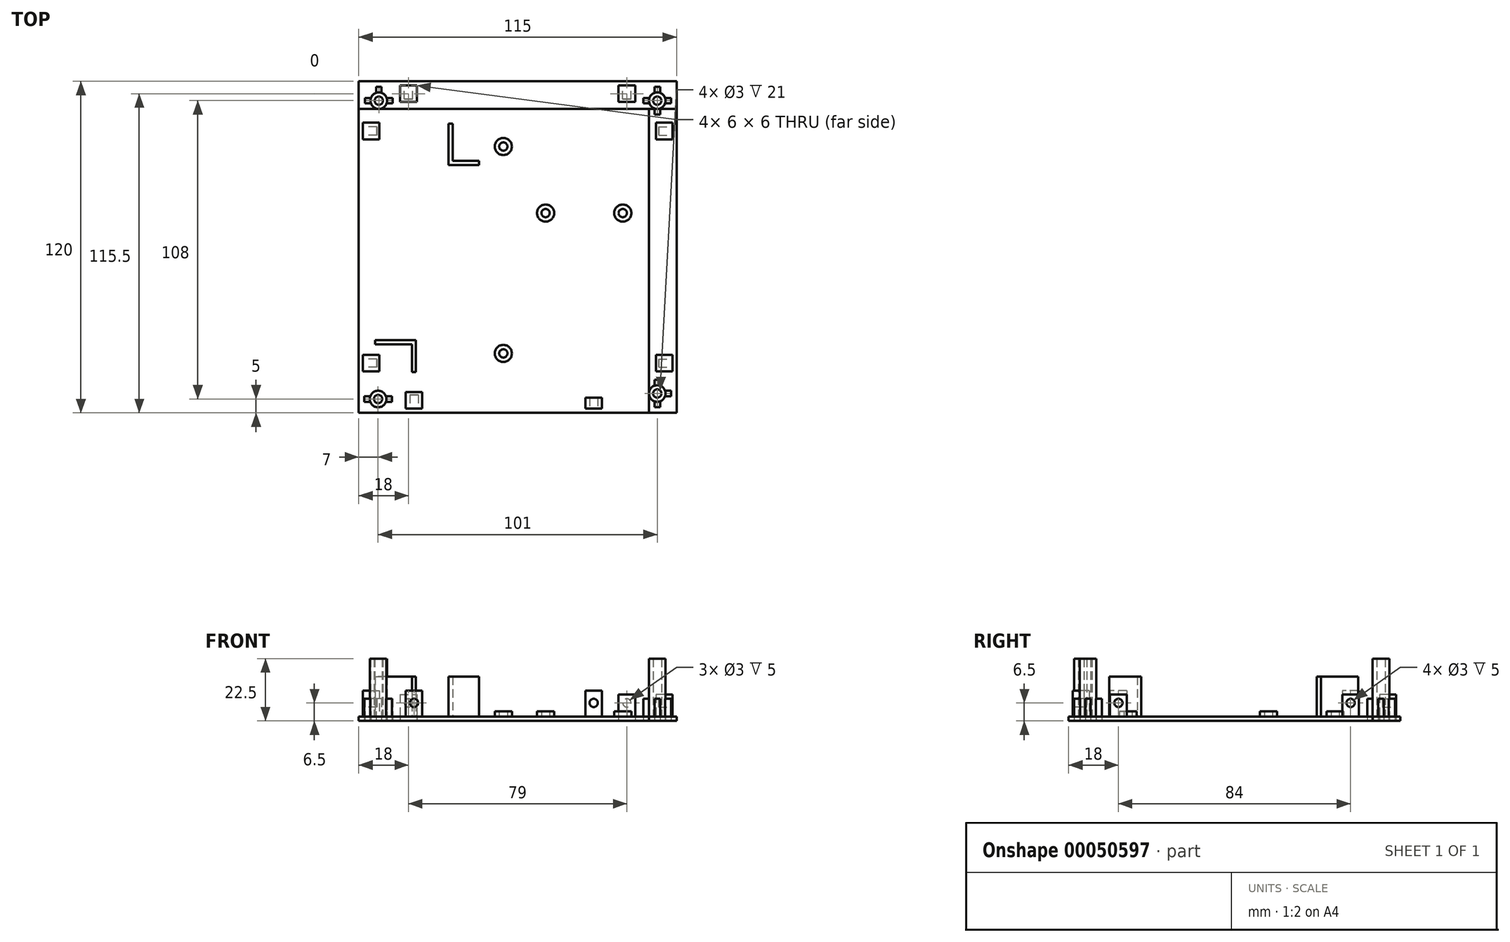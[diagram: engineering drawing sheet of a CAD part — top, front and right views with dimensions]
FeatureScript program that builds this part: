
annotation { "Feature Type Name" : "Feature", "Feature Type Description" : "" }
export const myFeature = defineFeature(function(context is Context, id is Id, definition is map)
    precondition{}
    {
        {
            var Q0;
            Q0=qCreatedBy(makeId("Top.planeOp"),FACE);
            var sketch = newSketch(context, id + "F0", { "sketchPlane" : qUnion([Q0])});
            skLineSegment(sketch, "E0.rect.bottom", {"start": v(52.5, 55) * mm, "end": v(-52.5, 55) * mm});
            skLineSegment(sketch, "E0.rect.top", {"start": v(52.5, -55) * mm, "end": v(-52.5, -55) * mm});
            skLineSegment(sketch, "E0.rect.left", {"start": v(52.5, 55) * mm, "end": v(52.5, -55) * mm});
            skLineSegment(sketch, "E0.rect.right", {"start": v(-52.5, 55) * mm, "end": v(-52.5, -55) * mm});
            skPoint(sketch, "E0.rect.middle", {"position": v(0, 0) * mm});
            skCircle(sketch, "E1", {"center": v(-45.5, -50) * mm, "radius": 3 * mm});
            skCircle(sketch, "E2", {"center": v(-45.5, -50) * mm, "radius": 1.5 * mm});
            skPoint(sketch, "E3.rect.middle", {"position": v(-45.5, -53) * mm});
            skLineSegment(sketch, "E4.rect.bottom", {"start": v(-50.5, -49) * mm, "end": v(-48.33, -49) * mm});
            skLineSegment(sketch, "E4.rect.top", {"start": v(-50.5, -51) * mm, "end": v(-48.33, -51) * mm});
            skLineSegment(sketch, "E4.rect.left", {"start": v(-50.5, -49) * mm, "end": v(-50.5, -51) * mm});
            skPoint(sketch, "E4.rect.middle", {"position": v(-48.5, -50) * mm});
            skLineSegment(sketch, "E5.rect.bottom", {"start": v(-40.5, -49) * mm, "end": v(-42.67, -49) * mm});
            skLineSegment(sketch, "E5.rect.top", {"start": v(-40.5, -51) * mm, "end": v(-42.67, -51) * mm});
            skLineSegment(sketch, "E5.rect.left", {"start": v(-40.5, -49) * mm, "end": v(-40.5, -51) * mm});
            skPoint(sketch, "E5.rect.middle", {"position": v(-42.5, -50) * mm});
            skPoint(sketch, "E4.rect.right.end.orphan", {"position": v(-46.5, -51) * mm});
            skPoint(sketch, "E6.trimOffspring.end.orphan", {"position": v(-46.5, -49) * mm});
            skPoint(sketch, "E7.orphan", {"position": v(-44.5, -49) * mm});
            skPoint(sketch, "E8.orphan", {"position": v(-44.5, -51) * mm});
            skSolve(sketch);
        }
        {
            var Q0;
            Q0=makeQuery(id+"F0.imprint","IMPRINT",FACE,{"disambiguationData":[TD([[makeQuery(id+"F0.imprint","IMPRINT",EDGE,{"derivedFrom":sQuery(id+"F0.wireOp",EDGE,"E0.rect.bottom")}),1.0]])]});
            extrude(context, id + "F1", {"entities" : qUnion([Q0]), "depth" : 1.5 * mm});
        }
        {
            var Q0;
            Q0=makeQuery(id+"F1.opExtrude","CAP_FACE",FACE,{"disambiguationData":[OSD([sQuery(id+"F0.wireOp",EDGE,"E0.rect.bottom"),sQuery(id+"F0.wireOp",EDGE,"E0.rect.top"),sQuery(id+"F0.wireOp",EDGE,"E0.rect.left"),sQuery(id+"F0.wireOp",EDGE,"E0.rect.right")])],"isStart":false});
            var sketch = newSketch(context, id + "F2", { "sketchPlane" : qUnion([Q0])});
            skCircle(sketch, "E9", {"center": v(-0.2, 41.4) * mm, "radius": 3.1 * mm});
            skCircle(sketch, "E10", {"center": v(-0.2, 41.4) * mm, "radius": 1.5 * mm});
            skCircle(sketch, "E11", {"center": v(-0.2, -33.5) * mm, "radius": 3.1 * mm});
            skCircle(sketch, "E12", {"center": v(-0.2, -33.5) * mm, "radius": 1.5 * mm});
            skCircle(sketch, "E13", {"center": v(43, 17.3) * mm, "radius": 3.1 * mm});
            skCircle(sketch, "E14", {"center": v(43, 17.3) * mm, "radius": 1.5 * mm});
            skCircle(sketch, "E15", {"center": v(15.1, 17.3) * mm, "radius": 3.1 * mm});
            skCircle(sketch, "E16", {"center": v(15.1, 17.3) * mm, "radius": 1.5 * mm});
            skLineSegment(sketch, "E17", {"start": v(-20, 49.73) * mm, "end": v(-20, 34.73) * mm});
            skLineSegment(sketch, "E18", {"start": v(-20, 34.73) * mm, "end": v(-9, 34.73) * mm});
            skLineSegment(sketch, "E19", {"start": v(-9, 34.73) * mm, "end": v(-9, 36.23) * mm});
            skLineSegment(sketch, "E20", {"start": v(-9, 36.23) * mm, "end": v(-18.5, 36.23) * mm});
            skLineSegment(sketch, "E21", {"start": v(-18.5, 36.23) * mm, "end": v(-18.5, 49.73) * mm});
            skLineSegment(sketch, "E22", {"start": v(-18.5, 49.73) * mm, "end": v(-20, 49.73) * mm});
            skLineSegment(sketch, "E23", {"start": v(-46.6, -28.7) * mm, "end": v(-31.8, -28.7) * mm});
            skLineSegment(sketch, "E24", {"start": v(-31.8, -28.7) * mm, "end": v(-31.8, -40.3) * mm});
            skLineSegment(sketch, "E25", {"start": v(-31.8, -40.3) * mm, "end": v(-33.3, -40.3) * mm});
            skLineSegment(sketch, "E26", {"start": v(-33.3, -40.3) * mm, "end": v(-33.3, -30.2) * mm});
            skLineSegment(sketch, "E27", {"start": v(-33.3, -30.2) * mm, "end": v(-46.6, -30.2) * mm});
            skLineSegment(sketch, "E28", {"start": v(-46.6, -30.2) * mm, "end": v(-46.6, -28.7) * mm});
            skSolve(sketch);
        }
        {
            var Q0;
            Q0=makeQuery(id+"F2.imprint","IMPRINT",FACE,{"disambiguationData":[TD([[makeQuery(id+"F2.imprint","IMPRINT",EDGE,{"derivedFrom":sQuery(id+"F2.wireOp",EDGE,"E9")}),1.0]])]});
            var Q1;
            Q1=makeQuery(id+"F2.imprint","IMPRINT",FACE,{"disambiguationData":[TD([[makeQuery(id+"F2.imprint","IMPRINT",EDGE,{"derivedFrom":sQuery(id+"F2.wireOp",EDGE,"E15")}),1.0]])]});
            var Q2;
            Q2=makeQuery(id+"F2.imprint","IMPRINT",FACE,{"disambiguationData":[TD([[makeQuery(id+"F2.imprint","IMPRINT",EDGE,{"derivedFrom":sQuery(id+"F2.wireOp",EDGE,"E13")}),1.0]])]});
            var Q3;
            Q3=makeQuery(id+"F2.imprint","IMPRINT",FACE,{"disambiguationData":[TD([[makeQuery(id+"F2.imprint","IMPRINT",EDGE,{"derivedFrom":sQuery(id+"F2.wireOp",EDGE,"E11")}),1.0]])]});
            extrude(context, id + "F3", {"entities" : qUnion([Q0, Q1, Q2, Q3]), "operationType" : NewBodyOperationType.ADD, "depth" : 2 * mm});
        }
        {
            var Q0;
            Q0=makeQuery(id+"F2.imprint","IMPRINT",FACE,{"disambiguationData":[TD([[makeQuery(id+"F2.imprint","IMPRINT",EDGE,{"derivedFrom":sQuery(id+"F2.wireOp",EDGE,"E17")}),1.0]])]});
            extrude(context, id + "F4", {"entities" : qUnion([Q0]), "operationType" : NewBodyOperationType.ADD, "depth" : 14.5 * mm});
        }
        {
            var Q0;
            Q0=makeQuery(id+"F2.imprint","IMPRINT",FACE,{"disambiguationData":[TD([[makeQuery(id+"F2.imprint","IMPRINT",EDGE,{"derivedFrom":sQuery(id+"F2.wireOp",EDGE,"E23")}),-1.0]])]});
            extrude(context, id + "F5", {"entities" : qUnion([Q0]), "operationType" : NewBodyOperationType.ADD, "depth" : 14.5 * mm});
        }
        {
            var Q0;
            Q0=qCreatedBy(makeId("Top.planeOp"),FACE);
            var sketch = newSketch(context, id + "F6", { "sketchPlane" : qUnion([Q0])});
            skLineSegment(sketch, "E29.bottom", {"start": v(-52.5, 55) * mm, "end": v(62.5, 55) * mm});
            skLineSegment(sketch, "E29.top", {"start": v(-52.5, 65) * mm, "end": v(62.5, 65) * mm});
            skLineSegment(sketch, "E29.left", {"start": v(-52.5, 55) * mm, "end": v(-52.5, 65) * mm});
            skLineSegment(sketch, "E29.right", {"start": v(62.5, 55) * mm, "end": v(62.5, 65) * mm});
            skLineSegment(sketch, "E30.bottom", {"start": v(62.5, 55) * mm, "end": v(52.5, 55) * mm});
            skLineSegment(sketch, "E30.top", {"start": v(62.5, -55) * mm, "end": v(52.5, -55) * mm});
            skLineSegment(sketch, "E30.left", {"start": v(62.5, 55) * mm, "end": v(62.5, -55) * mm});
            skLineSegment(sketch, "E30.right", {"start": v(52.5, 55) * mm, "end": v(52.5, -55) * mm});
            skCircle(sketch, "E31", {"center": v(-45.24, 58) * mm, "radius": 3 * mm});
            skCircle(sketch, "E32", {"center": v(-45.24, 58) * mm, "radius": 1.5 * mm});
            skLineSegment(sketch, "E33.rect.bottom", {"start": v(-44.24, 63) * mm, "end": v(-46.24, 63) * mm});
            skLineSegment(sketch, "E33.rect.left", {"start": v(-44.24, 63) * mm, "end": v(-44.24, 60.83) * mm});
            skLineSegment(sketch, "E33.rect.right", {"start": v(-46.24, 63) * mm, "end": v(-46.24, 60.83) * mm});
            skPoint(sketch, "E33.rect.middle", {"position": v(-45.24, 61) * mm});
            skLineSegment(sketch, "E34.rect.right", {"start": v(-50.24, 59) * mm, "end": v(-50.24, 57) * mm});
            skPoint(sketch, "E34.rect.middle", {"position": v(-48.24, 58) * mm});
            skLineSegment(sketch, "E35.rect.bottom", {"start": v(-44.24, 53) * mm, "end": v(-46.24, 53) * mm});
            skLineSegment(sketch, "E35.rect.left", {"start": v(-44.24, 53) * mm, "end": v(-44.24, 55.17) * mm});
            skLineSegment(sketch, "E35.rect.right", {"start": v(-46.24, 53) * mm, "end": v(-46.24, 55.17) * mm});
            skPoint(sketch, "E35.rect.middle", {"position": v(-45.24, 55) * mm});
            skLineSegment(sketch, "E36.rect.bottom", {"start": v(-40.24, 59) * mm, "end": v(-42.4, 59) * mm});
            skLineSegment(sketch, "E36.rect.top", {"start": v(-40.24, 57) * mm, "end": v(-42.4, 57) * mm});
            skLineSegment(sketch, "E36.rect.left", {"start": v(-40.24, 59) * mm, "end": v(-40.24, 57) * mm});
            skPoint(sketch, "E36.rect.middle", {"position": v(-42.24, 58) * mm});
            skPoint(sketch, "E37.trimOffspring.end.orphan", {"position": v(-44.24, 57) * mm});
            skLineSegment(sketch, "E38.trimOffspring", {"start": v(-48.06, 57) * mm, "end": v(-50.24, 57) * mm});
            skPoint(sketch, "E34.rect.top.start.orphan", {"position": v(-46.24, 57) * mm});
            skLineSegment(sketch, "E39.trimOffspring", {"start": v(-48.06, 59) * mm, "end": v(-50.24, 59) * mm});
            skPoint(sketch, "E34.rect.bottom.start.orphan", {"position": v(-46.24, 59) * mm});
            skPoint(sketch, "E40.orphan", {"position": v(-44.24, 59) * mm});
            skCircle(sketch, "E41", {"center": v(55.5, 58) * mm, "radius": 3 * mm});
            skCircle(sketch, "E42", {"center": v(55.5, 58) * mm, "radius": 1.5 * mm});
            skLineSegment(sketch, "E43.rect.bottom", {"start": v(56.5, 63) * mm, "end": v(54.5, 63) * mm});
            skLineSegment(sketch, "E43.rect.left", {"start": v(56.5, 63) * mm, "end": v(56.5, 60.83) * mm});
            skLineSegment(sketch, "E43.rect.right", {"start": v(54.5, 63) * mm, "end": v(54.5, 60.83) * mm});
            skPoint(sketch, "E43.rect.middle", {"position": v(55.5, 61) * mm});
            skLineSegment(sketch, "E44.rect.bottom", {"start": v(60.5, 59) * mm, "end": v(58.33, 59) * mm});
            skLineSegment(sketch, "E44.rect.top", {"start": v(60.5, 57) * mm, "end": v(58.33, 57) * mm});
            skLineSegment(sketch, "E44.rect.left", {"start": v(60.5, 59) * mm, "end": v(60.5, 57) * mm});
            skPoint(sketch, "E44.rect.middle", {"position": v(58.5, 58) * mm});
            skLineSegment(sketch, "E45.rect.bottom", {"start": v(56.5, 53) * mm, "end": v(54.5, 53) * mm});
            skLineSegment(sketch, "E45.rect.left", {"start": v(56.5, 53) * mm, "end": v(56.5, 55.17) * mm});
            skLineSegment(sketch, "E45.rect.right", {"start": v(54.5, 53) * mm, "end": v(54.5, 55.17) * mm});
            skPoint(sketch, "E45.rect.middle", {"position": v(55.5, 55) * mm});
            skLineSegment(sketch, "E46.rect.right", {"start": v(50.5, 59) * mm, "end": v(50.5, 57) * mm});
            skPoint(sketch, "E46.rect.middle", {"position": v(52.5, 58) * mm});
            skLineSegment(sketch, "E47.trimOffspring", {"start": v(52.67, 59) * mm, "end": v(50.5, 59) * mm});
            skLineSegment(sketch, "E48.trimOffspring", {"start": v(52.67, 57) * mm, "end": v(50.5, 57) * mm});
            skPoint(sketch, "E46.rect.bottom.start.orphan", {"position": v(54.5, 59) * mm});
            skPoint(sketch, "E46.rect.top.start.orphan", {"position": v(54.5, 57) * mm});
            skPoint(sketch, "E49.trimOffspring.end.orphan", {"position": v(56.5, 57) * mm});
            skPoint(sketch, "E50.orphan", {"position": v(56.5, 59) * mm});
            skCircle(sketch, "E51", {"center": v(55.5, -48) * mm, "radius": 3 * mm});
            skCircle(sketch, "E52", {"center": v(55.5, -48) * mm, "radius": 1.5 * mm});
            skLineSegment(sketch, "E53.rect.bottom", {"start": v(56.5, -53) * mm, "end": v(54.5, -53) * mm});
            skLineSegment(sketch, "E53.rect.left", {"start": v(56.5, -53) * mm, "end": v(56.5, -50.83) * mm});
            skLineSegment(sketch, "E53.rect.right", {"start": v(54.5, -53) * mm, "end": v(54.5, -50.83) * mm});
            skPoint(sketch, "E53.rect.middle", {"position": v(55.5, -51) * mm});
            skLineSegment(sketch, "E54.rect.bottom", {"start": v(60.5, -47) * mm, "end": v(58.33, -47) * mm});
            skLineSegment(sketch, "E54.rect.top", {"start": v(60.5, -49) * mm, "end": v(58.33, -49) * mm});
            skLineSegment(sketch, "E54.rect.left", {"start": v(60.5, -47) * mm, "end": v(60.5, -49) * mm});
            skPoint(sketch, "E54.rect.middle", {"position": v(58.5, -48) * mm});
            skLineSegment(sketch, "E55.rect.bottom", {"start": v(56.5, -43) * mm, "end": v(54.5, -43) * mm});
            skLineSegment(sketch, "E55.rect.left", {"start": v(56.5, -43) * mm, "end": v(56.5, -45.17) * mm});
            skLineSegment(sketch, "E55.rect.right", {"start": v(54.5, -43) * mm, "end": v(54.5, -45.17) * mm});
            skPoint(sketch, "E55.rect.middle", {"position": v(55.5, -45) * mm});
            skLineSegment(sketch, "E56.rect.right", {"start": v(50.5, -47) * mm, "end": v(50.5, -49) * mm});
            skPoint(sketch, "E56.rect.middle", {"position": v(52.5, -48) * mm});
            skLineSegment(sketch, "E57.trimOffspring", {"start": v(52.67, -49) * mm, "end": v(50.5, -49) * mm});
            skPoint(sketch, "E56.rect.top.start.orphan", {"position": v(54.5, -49) * mm});
            skPoint(sketch, "E58.trimOffspring.end.orphan", {"position": v(56.5, -49) * mm});
            skLineSegment(sketch, "E59.trimOffspring", {"start": v(52.67, -47) * mm, "end": v(50.5, -47) * mm});
            skPoint(sketch, "E56.rect.bottom.start.orphan", {"position": v(54.5, -47) * mm});
            skPoint(sketch, "E60.trimOffspring.end.orphan", {"position": v(56.5, -47) * mm});
            skLineSegment(sketch, "E61.bottom", {"start": v(-37.5, 63.5) * mm, "end": v(-31.5, 63.5) * mm});
            skLineSegment(sketch, "E61.top", {"start": v(-37.5, 57.5) * mm, "end": v(-31.5, 57.5) * mm});
            skLineSegment(sketch, "E61.left", {"start": v(-37.5, 63.5) * mm, "end": v(-37.5, 57.5) * mm});
            skLineSegment(sketch, "E61.right", {"start": v(-31.5, 63.5) * mm, "end": v(-31.5, 57.5) * mm});
            skLineSegment(sketch, "E62.bottom", {"start": v(41.5, 63.5) * mm, "end": v(47.5, 63.5) * mm});
            skLineSegment(sketch, "E62.top", {"start": v(41.5, 57.5) * mm, "end": v(47.5, 57.5) * mm});
            skLineSegment(sketch, "E62.left", {"start": v(41.5, 63.5) * mm, "end": v(41.5, 57.5) * mm});
            skLineSegment(sketch, "E62.right", {"start": v(47.5, 63.5) * mm, "end": v(47.5, 57.5) * mm});
            skLineSegment(sketch, "E63.rect.bottom", {"start": v(61, 44) * mm, "end": v(55, 44) * mm});
            skLineSegment(sketch, "E63.rect.top", {"start": v(61, 50) * mm, "end": v(55, 50) * mm});
            skLineSegment(sketch, "E63.rect.left", {"start": v(61, 44) * mm, "end": v(61, 50) * mm});
            skLineSegment(sketch, "E63.rect.right", {"start": v(55, 44) * mm, "end": v(55, 50) * mm});
            skPoint(sketch, "E63.rect.middle", {"position": v(58, 47) * mm});
            skLineSegment(sketch, "E64.rect.bottom", {"start": v(61, -40) * mm, "end": v(55, -40) * mm});
            skLineSegment(sketch, "E64.rect.top", {"start": v(61, -34) * mm, "end": v(55, -34) * mm});
            skLineSegment(sketch, "E64.rect.left", {"start": v(61, -40) * mm, "end": v(61, -34) * mm});
            skLineSegment(sketch, "E64.rect.right", {"start": v(55, -40) * mm, "end": v(55, -34) * mm});
            skPoint(sketch, "E64.rect.middle", {"position": v(58, -37) * mm});
            skSolve(sketch);
        }
        {
            var Q0;
            Q0=makeQuery(id+"F6.imprint","IMPRINT",FACE,{"disambiguationData":[TD([[makeQuery(id+"F6.imprint","IMPRINT",EDGE,{"derivedFrom":sQuery(id+"F6.wireOp",EDGE,"E29.bottom")}),1.0]])]});
            var Q1;
            Q1=makeQuery(id+"F6.imprint","IMPRINT",FACE,{"disambiguationData":[TD([[makeQuery(id+"F6.imprint","IMPRINT",EDGE,{"derivedFrom":sQuery(id+"F6.wireOp",EDGE,"E30.bottom")}),1.0]])]});
            extrude(context, id + "F7", {"entities" : qUnion([Q0, Q1]), "operationType" : NewBodyOperationType.ADD, "depth" : 1.5 * mm});
        }
        {
            var Q0;
            Q0=makeQuery(id+"F6.imprint","IMPRINT",FACE,{"disambiguationData":[TD([[makeQuery(id+"F6.imprint","IMPRINT",EDGE,{"derivedFrom":sQuery(id+"F6.wireOp",EDGE,"E32")}),-1.0]])]});
            extrude(context, id + "F8", {"entities" : qUnion([Q0]), "depth" : 22.5 * mm});
        }
        {
            var Q0;
            Q0=makeQuery(id+"F6.imprint","IMPRINT",FACE,{"disambiguationData":[TD([[makeQuery(id+"F6.imprint","IMPRINT",EDGE,{"derivedFrom":sQuery(id+"F6.wireOp",EDGE,"E33.rect.bottom")}),1.0]])]});
            var Q1;
            Q1=makeQuery(id+"F6.imprint","IMPRINT",FACE,{"disambiguationData":[TD([[makeQuery(id+"F6.imprint","IMPRINT",EDGE,{"derivedFrom":sQuery(id+"F6.wireOp",EDGE,"E34.rect.right")}),1.0]])]});
            var Q2;
            {var subQ0=sQuery(id+"F6.wireOp",EDGE,"E36.rect.bottom");Q2=makeQuery(id+"F6.imprint","IMPRINT",FACE,{"disambiguationData":[TD([[makeQuery(id+"F6.imprint","IMPRINT",EDGE,{"derivedFrom":subQ0}),1.0]])]});}
            extrude(context, id + "F9", {"entities" : qUnion([Q0, Q1, Q2]), "depth" : 8 * mm});
        }
        {
            var Q0;
            Q0=makeQuery(id+"F6.imprint","IMPRINT",FACE,{"disambiguationData":[TD([[makeQuery(id+"F6.imprint","IMPRINT",EDGE,{"derivedFrom":sQuery(id+"F6.wireOp",EDGE,"E42")}),-1.0]])]});
            extrude(context, id + "F10", {"entities" : qUnion([Q0]), "depth" : 22.5 * mm});
        }
        {
            var Q0;
            Q0=makeQuery(id+"F6.imprint","IMPRINT",FACE,{"disambiguationData":[TD([[makeQuery(id+"F6.imprint","IMPRINT",EDGE,{"derivedFrom":sQuery(id+"F6.wireOp",EDGE,"E46.rect.right")}),1.0]])]});
            var Q1;
            Q1=makeQuery(id+"F6.imprint","IMPRINT",FACE,{"disambiguationData":[TD([[makeQuery(id+"F6.imprint","IMPRINT",EDGE,{"derivedFrom":sQuery(id+"F6.wireOp",EDGE,"E43.rect.bottom")}),1.0]])]});
            var Q2;
            {var subQ0=sQuery(id+"F6.wireOp",EDGE,"E44.rect.bottom");Q2=makeQuery(id+"F6.imprint","IMPRINT",FACE,{"disambiguationData":[TD([[makeQuery(id+"F6.imprint","IMPRINT",EDGE,{"derivedFrom":subQ0}),1.0]])]});}
            var Q3;
            {var subQ0=sQuery(id+"F6.wireOp",EDGE,"E45.rect.bottom");Q3=makeQuery(id+"F6.imprint","IMPRINT",FACE,{"disambiguationData":[TD([[makeQuery(id+"F6.imprint","IMPRINT",EDGE,{"derivedFrom":subQ0}),-1.0]])]});}
            extrude(context, id + "F11", {"entities" : qUnion([Q0, Q1, Q2, Q3]), "depth" : 8 * mm});
        }
        {
            var Q0;
            Q0=makeQuery(id+"F6.imprint","IMPRINT",FACE,{"disambiguationData":[TD([[makeQuery(id+"F6.imprint","IMPRINT",EDGE,{"derivedFrom":sQuery(id+"F6.wireOp",EDGE,"E29.top")}),-1.0]])]});
            var Q1;
            Q1=makeQuery(id+"F6.imprint","IMPRINT",FACE,{"disambiguationData":[TD([[makeQuery(id+"F6.imprint","IMPRINT",EDGE,{"derivedFrom":sQuery(id+"F6.wireOp",EDGE,"E30.top")}),-1.0]])]});
            extrude(context, id + "F12", {"entities" : qUnion([Q0, Q1]), "depth" : 1.5 * mm});
        }
        {
            var Q0;
            Q0=makeQuery(id+"F6.imprint","IMPRINT",FACE,{"disambiguationData":[TD([[makeQuery(id+"F6.imprint","IMPRINT",EDGE,{"derivedFrom":sQuery(id+"F6.wireOp",EDGE,"E52")}),-1.0]])]});
            extrude(context, id + "F13", {"entities" : qUnion([Q0]), "depth" : 22.5 * mm});
        }
        {
            var Q0;
            Q0=makeQuery(id+"F6.imprint","IMPRINT",FACE,{"disambiguationData":[TD([[makeQuery(id+"F6.imprint","IMPRINT",EDGE,{"derivedFrom":sQuery(id+"F6.wireOp",EDGE,"E55.rect.bottom")}),1.0]])]});
            var Q1;
            {var subQ0=sQuery(id+"F6.wireOp",EDGE,"E54.rect.bottom");Q1=makeQuery(id+"F6.imprint","IMPRINT",FACE,{"disambiguationData":[TD([[makeQuery(id+"F6.imprint","IMPRINT",EDGE,{"derivedFrom":subQ0}),1.0]])]});}
            var Q2;
            Q2=makeQuery(id+"F6.imprint","IMPRINT",FACE,{"disambiguationData":[TD([[makeQuery(id+"F6.imprint","IMPRINT",EDGE,{"derivedFrom":sQuery(id+"F6.wireOp",EDGE,"E53.rect.bottom")}),-1.0]])]});
            extrude(context, id + "F14", {"entities" : qUnion([Q0, Q1, Q2]), "depth" : 8 * mm});
        }
        {
            var Q0;
            Q0=makeQuery(id+"F0.imprint","IMPRINT",FACE,{"disambiguationData":[TD([[makeQuery(id+"F0.imprint","IMPRINT",EDGE,{"derivedFrom":sQuery(id+"F0.wireOp",EDGE,"E2")}),-1.0]])]});
            extrude(context, id + "F15", {"entities" : qUnion([Q0]), "depth" : 22.5 * mm});
        }
        {
            var Q0;
            {var subQ0=sQuery(id+"F0.wireOp",EDGE,"E4.rect.bottom");Q0=makeQuery(id+"F0.imprint","IMPRINT",FACE,{"disambiguationData":[TD([[makeQuery(id+"F0.imprint","IMPRINT",EDGE,{"derivedFrom":subQ0}),-1.0]])]});}
            var Q1;
            {var subQ0=sQuery(id+"F0.wireOp",EDGE,"E5.rect.bottom");Q1=makeQuery(id+"F0.imprint","IMPRINT",FACE,{"disambiguationData":[TD([[makeQuery(id+"F0.imprint","IMPRINT",EDGE,{"derivedFrom":subQ0}),1.0]])]});}
            extrude(context, id + "F16", {"entities" : qUnion([Q0, Q1]), "depth" : 8 * mm});
        }
        {
            var Q0;
            Q0=makeQuery(id+"F6.imprint","IMPRINT",FACE,{"disambiguationData":[TD([[makeQuery(id+"F6.imprint","IMPRINT",EDGE,{"derivedFrom":sQuery(id+"F6.wireOp",EDGE,"E61.bottom")}),-1.0]])]});
            var Q1;
            Q1=makeQuery(id+"F6.imprint","IMPRINT",FACE,{"disambiguationData":[TD([[makeQuery(id+"F6.imprint","IMPRINT",EDGE,{"derivedFrom":sQuery(id+"F6.wireOp",EDGE,"E62.bottom")}),-1.0]])]});
            extrude(context, id + "F17", {"entities" : qUnion([Q0, Q1]), "depth" : 9.5 * mm});
        }
        {
            var Q0;
            Q0=makeQuery(id+"F6.imprint","IMPRINT",FACE,{"disambiguationData":[TD([[makeQuery(id+"F6.imprint","IMPRINT",EDGE,{"derivedFrom":sQuery(id+"F6.wireOp",EDGE,"E63.rect.bottom")}),-1.0]])]});
            var Q1;
            Q1=makeQuery(id+"F6.imprint","IMPRINT",FACE,{"disambiguationData":[TD([[makeQuery(id+"F6.imprint","IMPRINT",EDGE,{"derivedFrom":sQuery(id+"F6.wireOp",EDGE,"E64.rect.bottom")}),-1.0]])]});
            extrude(context, id + "F18", {"entities" : qUnion([Q0, Q1]), "operationType" : NewBodyOperationType.ADD, "depth" : 9.5 * mm});
        }
        {
            var Q0;
            Q0=makeQuery(id+"F18.opExtrude","SWEPT_FACE",FACE,{"disambiguationData":[OSD([sQuery(id+"F6.wireOp",EDGE,"E64.rect.left")])]});
            var sketch = newSketch(context, id + "F19", { "sketchPlane" : qUnion([Q0])});
            skCircle(sketch, "E65", {"center": v(-37, 6.5) * mm, "radius": 1.5 * mm});
            skSolve(sketch);
        }
        {
            var Q0;
            Q0=makeQuery(id+"F19.imprint","IMPRINT",FACE,{"disambiguationData":[TD([[makeQuery(id+"F19.imprint","IMPRINT",EDGE,{"derivedFrom":sQuery(id+"F19.wireOp",EDGE,"E65")}),1.0]])]});
            extrude(context, id + "F20", {"entities" : qUnion([Q0]), "operationType" : NewBodyOperationType.REMOVE, "oppositeDirection" : true, "depth" : 5 * mm});
        }
        {
            var Q0;
            Q0=makeQuery(id+"F18.opExtrude","SWEPT_FACE",FACE,{"disambiguationData":[OSD([sQuery(id+"F6.wireOp",EDGE,"E63.rect.left")])]});
            var sketch = newSketch(context, id + "F21", { "sketchPlane" : qUnion([Q0])});
            skCircle(sketch, "E66", {"center": v(47, 6.5) * mm, "radius": 1.5 * mm});
            skSolve(sketch);
        }
        {
            var Q0;
            Q0=makeQuery(id+"F21.imprint","IMPRINT",FACE,{"disambiguationData":[TD([[makeQuery(id+"F21.imprint","IMPRINT",EDGE,{"derivedFrom":sQuery(id+"F21.wireOp",EDGE,"E66")}),1.0]])]});
            extrude(context, id + "F22", {"entities" : qUnion([Q0]), "operationType" : NewBodyOperationType.REMOVE, "oppositeDirection" : true, "depth" : 5 * mm});
        }
        {
            var Q0;
            Q0=makeQuery(id+"F17.opExtrude","SWEPT_FACE",FACE,{"disambiguationData":[OSD([sQuery(id+"F6.wireOp",EDGE,"E62.bottom")])]});
            var sketch = newSketch(context, id + "F23", { "sketchPlane" : qUnion([Q0])});
            skCircle(sketch, "E67", {"center": v(-44.5, 6.5) * mm, "radius": 1.5 * mm});
            skSolve(sketch);
        }
        {
            var Q0;
            Q0=makeQuery(id+"F23.imprint","IMPRINT",FACE,{"disambiguationData":[TD([[makeQuery(id+"F23.imprint","IMPRINT",EDGE,{"derivedFrom":sQuery(id+"F23.wireOp",EDGE,"E67")}),1.0]])]});
            extrude(context, id + "F24", {"entities" : qUnion([Q0]), "operationType" : NewBodyOperationType.REMOVE, "oppositeDirection" : true, "depth" : 5 * mm});
        }
        {
            var Q0;
            Q0=makeQuery(id+"F17.opExtrude","SWEPT_FACE",FACE,{"disambiguationData":[OSD([sQuery(id+"F6.wireOp",EDGE,"E61.bottom")])]});
            var sketch = newSketch(context, id + "F25", { "sketchPlane" : qUnion([Q0])});
            skCircle(sketch, "E68", {"center": v(34.5, 6.5) * mm, "radius": 1.5 * mm});
            skPoint(sketch, "E68.centerSnap0", {"position": v(34.5, 9.5) * mm});
            skSolve(sketch);
        }
        {
            var Q0;
            Q0=makeQuery(id+"F25.imprint","IMPRINT",FACE,{"disambiguationData":[TD([[makeQuery(id+"F25.imprint","IMPRINT",EDGE,{"derivedFrom":sQuery(id+"F25.wireOp",EDGE,"E68")}),1.0]])]});
            extrude(context, id + "F26", {"entities" : qUnion([Q0]), "operationType" : NewBodyOperationType.REMOVE, "oppositeDirection" : true, "depth" : 5 * mm});
        }
        {
            var Q0;
            {var subQ0=sQuery(id+"F6.wireOp",EDGE,"E64.rect.right");var subQ1=sQuery(id+"F6.wireOp",EDGE,"E64.rect.left");var subQ2=sQuery(id+"F6.wireOp",EDGE,"E64.rect.top");var subQ3=sQuery(id+"F6.wireOp",EDGE,"E64.rect.bottom");var subQ4=sQuery(id+"F6.wireOp",EDGE,"E63.rect.right");var subQ5=sQuery(id+"F6.wireOp",EDGE,"E63.rect.left");var subQ6=sQuery(id+"F6.wireOp",EDGE,"E63.rect.top");var subQ7=sQuery(id+"F6.wireOp",EDGE,"E63.rect.bottom");Q0=makeQuery(id+"F18.boolean.opBoolean","MERGE",FACE,{"derivedFrom":[makeQuery(id+"F12.opExtrude","CAP_FACE",FACE,{"disambiguationData":[OSD([sQuery(id+"F6.wireOp",EDGE,"E29.bottom"),sQuery(id+"F6.wireOp",EDGE,"E29.top"),sQuery(id+"F6.wireOp",EDGE,"E29.left"),sQuery(id+"F6.wireOp",EDGE,"E29.right"),sQuery(id+"F6.wireOp",EDGE,"E30.top"),sQuery(id+"F6.wireOp",EDGE,"E30.left"),sQuery(id+"F6.wireOp",EDGE,"E30.right"),sQuery(id+"F6.wireOp",EDGE,"E31"),sQuery(id+"F6.wireOp",EDGE,"E33.rect.bottom"),sQuery(id+"F6.wireOp",EDGE,"E33.rect.left"),sQuery(id+"F6.wireOp",EDGE,"E33.rect.right"),sQuery(id+"F6.wireOp",EDGE,"E34.rect.right"),sQuery(id+"F6.wireOp",EDGE,"E35.rect.left"),sQuery(id+"F6.wireOp",EDGE,"E35.rect.right"),sQuery(id+"F6.wireOp",EDGE,"E36.rect.bottom"),sQuery(id+"F6.wireOp",EDGE,"E36.rect.top"),sQuery(id+"F6.wireOp",EDGE,"E36.rect.left"),sQuery(id+"F6.wireOp",EDGE,"E38.trimOffspring"),sQuery(id+"F6.wireOp",EDGE,"E39.trimOffspring"),sQuery(id+"F6.wireOp",EDGE,"E41"),sQuery(id+"F6.wireOp",EDGE,"E43.rect.bottom"),sQuery(id+"F6.wireOp",EDGE,"E43.rect.left"),sQuery(id+"F6.wireOp",EDGE,"E43.rect.right"),sQuery(id+"F6.wireOp",EDGE,"E44.rect.bottom"),sQuery(id+"F6.wireOp",EDGE,"E44.rect.top"),sQuery(id+"F6.wireOp",EDGE,"E44.rect.left"),sQuery(id+"F6.wireOp",EDGE,"E45.rect.bottom"),sQuery(id+"F6.wireOp",EDGE,"E45.rect.left"),sQuery(id+"F6.wireOp",EDGE,"E45.rect.right"),sQuery(id+"F6.wireOp",EDGE,"E46.rect.right"),sQuery(id+"F6.wireOp",EDGE,"E47.trimOffspring"),sQuery(id+"F6.wireOp",EDGE,"E48.trimOffspring"),sQuery(id+"F6.wireOp",EDGE,"E51"),sQuery(id+"F6.wireOp",EDGE,"E53.rect.bottom"),sQuery(id+"F6.wireOp",EDGE,"E53.rect.left"),sQuery(id+"F6.wireOp",EDGE,"E53.rect.right"),sQuery(id+"F6.wireOp",EDGE,"E54.rect.bottom"),sQuery(id+"F6.wireOp",EDGE,"E54.rect.top"),sQuery(id+"F6.wireOp",EDGE,"E54.rect.left"),sQuery(id+"F6.wireOp",EDGE,"E55.rect.bottom"),sQuery(id+"F6.wireOp",EDGE,"E55.rect.left"),sQuery(id+"F6.wireOp",EDGE,"E55.rect.right"),sQuery(id+"F6.wireOp",EDGE,"E57.trimOffspring"),sQuery(id+"F6.wireOp",EDGE,"E59.trimOffspring"),sQuery(id+"F6.wireOp",EDGE,"E61.bottom"),sQuery(id+"F6.wireOp",EDGE,"E61.top"),sQuery(id+"F6.wireOp",EDGE,"E61.left"),sQuery(id+"F6.wireOp",EDGE,"E61.right"),sQuery(id+"F6.wireOp",EDGE,"E62.bottom"),sQuery(id+"F6.wireOp",EDGE,"E62.top"),sQuery(id+"F6.wireOp",EDGE,"E62.left"),sQuery(id+"F6.wireOp",EDGE,"E62.right"),subQ7,subQ6,subQ5,subQ4,subQ3,subQ2,subQ1,subQ0])],"isStart":true}),makeQuery(id+"F18.opExtrude","CAP_FACE",FACE,{"disambiguationData":[OSD([subQ7,subQ6,subQ5,subQ4])],"isStart":true}),makeQuery(id+"F18.opExtrude","CAP_FACE",FACE,{"disambiguationData":[OSD([subQ3,subQ2,subQ1,subQ0])],"isStart":true})]});}
            var sketch = newSketch(context, id + "F27", { "sketchPlane" : qUnion([Q0])});
            skCircle(sketch, "E69", {"center": v(55.5, 48) * mm, "radius": 1.75 * mm});
            skSolve(sketch);
        }
        {
            var Q0;
            Q0=makeQuery(id+"F27.imprint","IMPRINT",FACE,{"disambiguationData":[TD([[makeQuery(id+"F27.imprint","IMPRINT",EDGE,{"derivedFrom":sQuery(id+"F27.wireOp",EDGE,"E69")}),1.0]])]});
            extrude(context, id + "F28", {"entities" : qUnion([Q0]), "operationType" : NewBodyOperationType.ADD, "oppositeDirection" : true, "depth" : 1.5 * mm});
        }
        {
            var Q0;
            {var subQ0=sQuery(id+"F6.wireOp",EDGE,"E64.rect.right");var subQ1=sQuery(id+"F6.wireOp",EDGE,"E64.rect.left");var subQ2=sQuery(id+"F6.wireOp",EDGE,"E64.rect.top");var subQ3=sQuery(id+"F6.wireOp",EDGE,"E64.rect.bottom");var subQ4=sQuery(id+"F6.wireOp",EDGE,"E63.rect.right");var subQ5=sQuery(id+"F6.wireOp",EDGE,"E63.rect.left");var subQ6=sQuery(id+"F6.wireOp",EDGE,"E63.rect.top");var subQ7=sQuery(id+"F6.wireOp",EDGE,"E63.rect.bottom");Q0=makeQuery(id+"F18.boolean.opBoolean","MERGE",FACE,{"derivedFrom":[makeQuery(id+"F12.opExtrude","CAP_FACE",FACE,{"disambiguationData":[OSD([sQuery(id+"F6.wireOp",EDGE,"E29.bottom"),sQuery(id+"F6.wireOp",EDGE,"E29.top"),sQuery(id+"F6.wireOp",EDGE,"E29.left"),sQuery(id+"F6.wireOp",EDGE,"E29.right"),sQuery(id+"F6.wireOp",EDGE,"E30.top"),sQuery(id+"F6.wireOp",EDGE,"E30.left"),sQuery(id+"F6.wireOp",EDGE,"E30.right"),sQuery(id+"F6.wireOp",EDGE,"E31"),sQuery(id+"F6.wireOp",EDGE,"E33.rect.bottom"),sQuery(id+"F6.wireOp",EDGE,"E33.rect.left"),sQuery(id+"F6.wireOp",EDGE,"E33.rect.right"),sQuery(id+"F6.wireOp",EDGE,"E34.rect.right"),sQuery(id+"F6.wireOp",EDGE,"E35.rect.left"),sQuery(id+"F6.wireOp",EDGE,"E35.rect.right"),sQuery(id+"F6.wireOp",EDGE,"E36.rect.bottom"),sQuery(id+"F6.wireOp",EDGE,"E36.rect.top"),sQuery(id+"F6.wireOp",EDGE,"E36.rect.left"),sQuery(id+"F6.wireOp",EDGE,"E38.trimOffspring"),sQuery(id+"F6.wireOp",EDGE,"E39.trimOffspring"),sQuery(id+"F6.wireOp",EDGE,"E41"),sQuery(id+"F6.wireOp",EDGE,"E43.rect.bottom"),sQuery(id+"F6.wireOp",EDGE,"E43.rect.left"),sQuery(id+"F6.wireOp",EDGE,"E43.rect.right"),sQuery(id+"F6.wireOp",EDGE,"E44.rect.bottom"),sQuery(id+"F6.wireOp",EDGE,"E44.rect.top"),sQuery(id+"F6.wireOp",EDGE,"E44.rect.left"),sQuery(id+"F6.wireOp",EDGE,"E45.rect.bottom"),sQuery(id+"F6.wireOp",EDGE,"E45.rect.left"),sQuery(id+"F6.wireOp",EDGE,"E45.rect.right"),sQuery(id+"F6.wireOp",EDGE,"E46.rect.right"),sQuery(id+"F6.wireOp",EDGE,"E47.trimOffspring"),sQuery(id+"F6.wireOp",EDGE,"E48.trimOffspring"),sQuery(id+"F6.wireOp",EDGE,"E51"),sQuery(id+"F6.wireOp",EDGE,"E53.rect.bottom"),sQuery(id+"F6.wireOp",EDGE,"E53.rect.left"),sQuery(id+"F6.wireOp",EDGE,"E53.rect.right"),sQuery(id+"F6.wireOp",EDGE,"E54.rect.bottom"),sQuery(id+"F6.wireOp",EDGE,"E54.rect.top"),sQuery(id+"F6.wireOp",EDGE,"E54.rect.left"),sQuery(id+"F6.wireOp",EDGE,"E55.rect.bottom"),sQuery(id+"F6.wireOp",EDGE,"E55.rect.left"),sQuery(id+"F6.wireOp",EDGE,"E55.rect.right"),sQuery(id+"F6.wireOp",EDGE,"E57.trimOffspring"),sQuery(id+"F6.wireOp",EDGE,"E59.trimOffspring"),sQuery(id+"F6.wireOp",EDGE,"E61.bottom"),sQuery(id+"F6.wireOp",EDGE,"E61.top"),sQuery(id+"F6.wireOp",EDGE,"E61.left"),sQuery(id+"F6.wireOp",EDGE,"E61.right"),sQuery(id+"F6.wireOp",EDGE,"E62.bottom"),sQuery(id+"F6.wireOp",EDGE,"E62.top"),sQuery(id+"F6.wireOp",EDGE,"E62.left"),sQuery(id+"F6.wireOp",EDGE,"E62.right"),subQ7,subQ6,subQ5,subQ4,subQ3,subQ2,subQ1,subQ0])],"isStart":true}),makeQuery(id+"F18.opExtrude","CAP_FACE",FACE,{"disambiguationData":[OSD([subQ7,subQ6,subQ5,subQ4])],"isStart":true}),makeQuery(id+"F18.opExtrude","CAP_FACE",FACE,{"disambiguationData":[OSD([subQ3,subQ2,subQ1,subQ0])],"isStart":true})]});}
            var sketch = newSketch(context, id + "F29", { "sketchPlane" : qUnion([Q0])});
            skCircle(sketch, "E70", {"center": v(55.5, -58) * mm, "radius": 1.75 * mm});
            skSolve(sketch);
        }
        {
            var Q0;
            Q0=makeQuery(id+"F29.imprint","IMPRINT",FACE,{"disambiguationData":[TD([[makeQuery(id+"F29.imprint","IMPRINT",EDGE,{"derivedFrom":sQuery(id+"F29.wireOp",EDGE,"E70")}),1.0]])]});
            extrude(context, id + "F30", {"entities" : qUnion([Q0]), "operationType" : NewBodyOperationType.ADD, "oppositeDirection" : true, "depth" : 1.5 * mm});
        }
        {
            var Q0;
            {var subQ0=sQuery(id+"F6.wireOp",EDGE,"E64.rect.right");var subQ1=sQuery(id+"F6.wireOp",EDGE,"E64.rect.left");var subQ2=sQuery(id+"F6.wireOp",EDGE,"E64.rect.top");var subQ3=sQuery(id+"F6.wireOp",EDGE,"E64.rect.bottom");var subQ4=sQuery(id+"F6.wireOp",EDGE,"E63.rect.right");var subQ5=sQuery(id+"F6.wireOp",EDGE,"E63.rect.left");var subQ6=sQuery(id+"F6.wireOp",EDGE,"E63.rect.top");var subQ7=sQuery(id+"F6.wireOp",EDGE,"E63.rect.bottom");Q0=makeQuery(id+"F18.boolean.opBoolean","MERGE",FACE,{"derivedFrom":[makeQuery(id+"F12.opExtrude","CAP_FACE",FACE,{"disambiguationData":[OSD([sQuery(id+"F6.wireOp",EDGE,"E29.bottom"),sQuery(id+"F6.wireOp",EDGE,"E29.top"),sQuery(id+"F6.wireOp",EDGE,"E29.left"),sQuery(id+"F6.wireOp",EDGE,"E29.right"),sQuery(id+"F6.wireOp",EDGE,"E30.top"),sQuery(id+"F6.wireOp",EDGE,"E30.left"),sQuery(id+"F6.wireOp",EDGE,"E30.right"),sQuery(id+"F6.wireOp",EDGE,"E31"),sQuery(id+"F6.wireOp",EDGE,"E33.rect.bottom"),sQuery(id+"F6.wireOp",EDGE,"E33.rect.left"),sQuery(id+"F6.wireOp",EDGE,"E33.rect.right"),sQuery(id+"F6.wireOp",EDGE,"E34.rect.right"),sQuery(id+"F6.wireOp",EDGE,"E35.rect.left"),sQuery(id+"F6.wireOp",EDGE,"E35.rect.right"),sQuery(id+"F6.wireOp",EDGE,"E36.rect.bottom"),sQuery(id+"F6.wireOp",EDGE,"E36.rect.top"),sQuery(id+"F6.wireOp",EDGE,"E36.rect.left"),sQuery(id+"F6.wireOp",EDGE,"E38.trimOffspring"),sQuery(id+"F6.wireOp",EDGE,"E39.trimOffspring"),sQuery(id+"F6.wireOp",EDGE,"E41"),sQuery(id+"F6.wireOp",EDGE,"E43.rect.bottom"),sQuery(id+"F6.wireOp",EDGE,"E43.rect.left"),sQuery(id+"F6.wireOp",EDGE,"E43.rect.right"),sQuery(id+"F6.wireOp",EDGE,"E44.rect.bottom"),sQuery(id+"F6.wireOp",EDGE,"E44.rect.top"),sQuery(id+"F6.wireOp",EDGE,"E44.rect.left"),sQuery(id+"F6.wireOp",EDGE,"E45.rect.bottom"),sQuery(id+"F6.wireOp",EDGE,"E45.rect.left"),sQuery(id+"F6.wireOp",EDGE,"E45.rect.right"),sQuery(id+"F6.wireOp",EDGE,"E46.rect.right"),sQuery(id+"F6.wireOp",EDGE,"E47.trimOffspring"),sQuery(id+"F6.wireOp",EDGE,"E48.trimOffspring"),sQuery(id+"F6.wireOp",EDGE,"E51"),sQuery(id+"F6.wireOp",EDGE,"E53.rect.bottom"),sQuery(id+"F6.wireOp",EDGE,"E53.rect.left"),sQuery(id+"F6.wireOp",EDGE,"E53.rect.right"),sQuery(id+"F6.wireOp",EDGE,"E54.rect.bottom"),sQuery(id+"F6.wireOp",EDGE,"E54.rect.top"),sQuery(id+"F6.wireOp",EDGE,"E54.rect.left"),sQuery(id+"F6.wireOp",EDGE,"E55.rect.bottom"),sQuery(id+"F6.wireOp",EDGE,"E55.rect.left"),sQuery(id+"F6.wireOp",EDGE,"E55.rect.right"),sQuery(id+"F6.wireOp",EDGE,"E57.trimOffspring"),sQuery(id+"F6.wireOp",EDGE,"E59.trimOffspring"),sQuery(id+"F6.wireOp",EDGE,"E61.bottom"),sQuery(id+"F6.wireOp",EDGE,"E61.top"),sQuery(id+"F6.wireOp",EDGE,"E61.left"),sQuery(id+"F6.wireOp",EDGE,"E61.right"),sQuery(id+"F6.wireOp",EDGE,"E62.bottom"),sQuery(id+"F6.wireOp",EDGE,"E62.top"),sQuery(id+"F6.wireOp",EDGE,"E62.left"),sQuery(id+"F6.wireOp",EDGE,"E62.right"),subQ7,subQ6,subQ5,subQ4,subQ3,subQ2,subQ1,subQ0])],"isStart":true}),makeQuery(id+"F18.opExtrude","CAP_FACE",FACE,{"disambiguationData":[OSD([subQ7,subQ6,subQ5,subQ4])],"isStart":true}),makeQuery(id+"F18.opExtrude","CAP_FACE",FACE,{"disambiguationData":[OSD([subQ3,subQ2,subQ1,subQ0])],"isStart":true})]});}
            var sketch = newSketch(context, id + "F31", { "sketchPlane" : qUnion([Q0])});
            skCircle(sketch, "E71", {"center": v(-45.24, -58) * mm, "radius": 1.75 * mm});
            skSolve(sketch);
        }
        {
            var Q0;
            Q0=makeQuery(id+"F31.imprint","IMPRINT",FACE,{"disambiguationData":[TD([[makeQuery(id+"F31.imprint","IMPRINT",EDGE,{"derivedFrom":sQuery(id+"F31.wireOp",EDGE,"E71")}),1.0]])]});
            extrude(context, id + "F32", {"entities" : qUnion([Q0]), "operationType" : NewBodyOperationType.ADD, "oppositeDirection" : true, "depth" : 1.5 * mm});
        }
        {
            var Q0;
            {var subQ0=sQuery(id+"F6.wireOp",EDGE,"E31");var subQ1=sQuery(id+"F6.wireOp",EDGE,"E29.bottom");Q0=makeQuery(id+"F7.boolean.opBoolean","MERGE",FACE,{"derivedFrom":[makeQuery(id+"F1.opExtrude","CAP_FACE",FACE,{"disambiguationData":[OSD([sQuery(id+"F0.wireOp",EDGE,"E0.rect.bottom"),sQuery(id+"F0.wireOp",EDGE,"E0.rect.top"),sQuery(id+"F0.wireOp",EDGE,"E0.rect.left"),sQuery(id+"F0.wireOp",EDGE,"E0.rect.right"),sQuery(id+"F0.wireOp",EDGE,"E1"),sQuery(id+"F0.wireOp",EDGE,"E4.rect.bottom"),sQuery(id+"F0.wireOp",EDGE,"E4.rect.top"),sQuery(id+"F0.wireOp",EDGE,"E4.rect.left"),sQuery(id+"F0.wireOp",EDGE,"E5.rect.bottom"),sQuery(id+"F0.wireOp",EDGE,"E5.rect.top"),sQuery(id+"F0.wireOp",EDGE,"E5.rect.left")])],"isStart":true}),makeQuery(id+"F7.opExtrude","CAP_FACE",FACE,{"disambiguationData":[OSD([subQ1,subQ0,sQuery(id+"F6.wireOp",EDGE,"E35.rect.right")])],"isStart":true}),makeQuery(id+"F7.opExtrude","CAP_FACE",FACE,{"disambiguationData":[OSD([subQ1,subQ0,sQuery(id+"F6.wireOp",EDGE,"E35.rect.left")])],"isStart":true})]});}
            var sketch = newSketch(context, id + "F33", { "sketchPlane" : qUnion([Q0])});
            skCircle(sketch, "E72", {"center": v(-45.5, 50) * mm, "radius": 1.75 * mm});
            skSolve(sketch);
        }
        {
            var Q0;
            Q0=makeQuery(id+"F33.imprint","IMPRINT",FACE,{"disambiguationData":[TD([[makeQuery(id+"F33.imprint","IMPRINT",EDGE,{"derivedFrom":sQuery(id+"F33.wireOp",EDGE,"E72")}),1.0]])]});
            extrude(context, id + "F34", {"entities" : qUnion([Q0]), "operationType" : NewBodyOperationType.ADD, "oppositeDirection" : true, "depth" : 1.5 * mm});
        }
        {
            var Q0;
            {var subQ0=sQuery(id+"F6.wireOp",EDGE,"E31");var subQ1=sQuery(id+"F6.wireOp",EDGE,"E29.bottom");var subQ2=sQuery(id+"F0.wireOp",EDGE,"E5.rect.bottom");var subQ3=sQuery(id+"F0.wireOp",EDGE,"E4.rect.top");var subQ4=sQuery(id+"F0.wireOp",EDGE,"E4.rect.bottom");var subQ5=sQuery(id+"F0.wireOp",EDGE,"E1");var subQ6=sQuery(id+"F0.wireOp",EDGE,"E5.rect.top");var subQ7=sQuery(id+"F0.wireOp",EDGE,"E0.rect.bottom");var subQ8=sQuery(id+"F0.wireOp",EDGE,"E4.rect.left");var subQ9=sQuery(id+"F0.wireOp",EDGE,"E0.rect.top");var subQ10=sQuery(id+"F0.wireOp",EDGE,"E0.rect.left");var subQ11=sQuery(id+"F0.wireOp",EDGE,"E0.rect.right");var subQ12=sQuery(id+"F0.wireOp",EDGE,"E5.rect.left");Q0=makeQuery(id+"F7.boolean.opBoolean","MERGE",FACE,{"derivedFrom":[makeQuery(id+"F3.boolean.opBoolean","SPLIT",FACE,{"disambiguationData":[TD([makeQuery(id+"F1.opExtrude","SWEPT_FACE",FACE,{"disambiguationData":[OSD([subQ7])]})])],"derivedFrom":makeQuery(id+"F1.opExtrude","CAP_FACE",FACE,{"disambiguationData":[OSD([subQ7,subQ9,subQ10,subQ11,subQ5,subQ4,subQ3,subQ8,subQ2,subQ6,subQ12])],"isStart":false})}),makeQuery(id+"F7.opExtrude","CAP_FACE",FACE,{"disambiguationData":[OSD([subQ1,subQ0,sQuery(id+"F6.wireOp",EDGE,"E35.rect.right")])],"isStart":false}),makeQuery(id+"F7.opExtrude","CAP_FACE",FACE,{"disambiguationData":[OSD([subQ1,subQ0,sQuery(id+"F6.wireOp",EDGE,"E35.rect.left")])],"isStart":false})]});}
            var sketch = newSketch(context, id + "F35", { "sketchPlane" : qUnion([Q0])});
            skLineSegment(sketch, "E73.bottom", {"start": v(29.5, -49.5) * mm, "end": v(35.5, -49.5) * mm});
            skLineSegment(sketch, "E73.top", {"start": v(29.5, -53.5) * mm, "end": v(35.5, -53.5) * mm});
            skLineSegment(sketch, "E73.left", {"start": v(29.5, -49.5) * mm, "end": v(29.5, -53.5) * mm});
            skLineSegment(sketch, "E73.right", {"start": v(35.5, -49.5) * mm, "end": v(35.5, -53.5) * mm});
            skLineSegment(sketch, "E74.bottom", {"start": v(-35.5, -47.5) * mm, "end": v(-29.5, -47.5) * mm});
            skLineSegment(sketch, "E74.top", {"start": v(-35.5, -53.5) * mm, "end": v(-29.5, -53.5) * mm});
            skLineSegment(sketch, "E74.left", {"start": v(-35.5, -47.5) * mm, "end": v(-35.5, -53.5) * mm});
            skLineSegment(sketch, "E74.right", {"start": v(-29.5, -47.5) * mm, "end": v(-29.5, -53.5) * mm});
            skSolve(sketch);
        }
        {
            var Q0;
            Q0=makeQuery(id+"F35.imprint","IMPRINT",FACE,{"disambiguationData":[TD([[makeQuery(id+"F35.imprint","IMPRINT",EDGE,{"derivedFrom":sQuery(id+"F35.wireOp",EDGE,"E74.bottom")}),-1.0]])]});
            var Q1;
            Q1=makeQuery(id+"F35.imprint","IMPRINT",FACE,{"disambiguationData":[TD([[makeQuery(id+"F35.imprint","IMPRINT",EDGE,{"derivedFrom":sQuery(id+"F35.wireOp",EDGE,"E73.bottom")}),-1.0]])]});
            extrude(context, id + "F36", {"entities" : qUnion([Q0, Q1]), "operationType" : NewBodyOperationType.ADD, "depth" : 9.5 * mm});
        }
        {
            var Q0;
            Q0=makeQuery(id+"F36.opExtrude","SWEPT_FACE",FACE,{"disambiguationData":[OSD([sQuery(id+"F35.wireOp",EDGE,"E74.top")])]});
            var sketch = newSketch(context, id + "F37", { "sketchPlane" : qUnion([Q0])});
            skCircle(sketch, "E75", {"center": v(-32.5, 6.5) * mm, "radius": 1.5 * mm});
            skSolve(sketch);
        }
        {
            var Q0;
            Q0=makeQuery(id+"F37.imprint","IMPRINT",FACE,{"disambiguationData":[TD([[makeQuery(id+"F37.imprint","IMPRINT",EDGE,{"derivedFrom":sQuery(id+"F37.wireOp",EDGE,"E75")}),1.0]])]});
            extrude(context, id + "F38", {"entities" : qUnion([Q0]), "operationType" : NewBodyOperationType.REMOVE, "oppositeDirection" : true, "depth" : 5 * mm});
        }
        {
            var Q0;
            Q0=makeQuery(id+"F36.opExtrude","SWEPT_FACE",FACE,{"disambiguationData":[OSD([sQuery(id+"F35.wireOp",EDGE,"E73.top")])]});
            var sketch = newSketch(context, id + "F39", { "sketchPlane" : qUnion([Q0])});
            skCircle(sketch, "E76", {"center": v(32.5, 6.5) * mm, "radius": 1.5 * mm});
            skSolve(sketch);
        }
        {
            var Q0;
            Q0=makeQuery(id+"F39.imprint","IMPRINT",FACE,{"disambiguationData":[TD([[makeQuery(id+"F39.imprint","IMPRINT",EDGE,{"derivedFrom":sQuery(id+"F39.wireOp",EDGE,"E76")}),1.0]])]});
            extrude(context, id + "F40", {"entities" : qUnion([Q0]), "operationType" : NewBodyOperationType.REMOVE, "oppositeDirection" : true, "depth" : 5 * mm});
        }
        {
            var Q0;
            {var subQ0=sQuery(id+"F6.wireOp",EDGE,"E31");var subQ1=sQuery(id+"F6.wireOp",EDGE,"E29.bottom");var subQ2=sQuery(id+"F0.wireOp",EDGE,"E5.rect.bottom");var subQ3=sQuery(id+"F0.wireOp",EDGE,"E4.rect.top");var subQ4=sQuery(id+"F0.wireOp",EDGE,"E4.rect.bottom");var subQ5=sQuery(id+"F0.wireOp",EDGE,"E1");var subQ6=sQuery(id+"F0.wireOp",EDGE,"E5.rect.top");var subQ7=sQuery(id+"F0.wireOp",EDGE,"E0.rect.bottom");var subQ8=sQuery(id+"F0.wireOp",EDGE,"E4.rect.left");var subQ9=sQuery(id+"F0.wireOp",EDGE,"E0.rect.top");var subQ10=sQuery(id+"F0.wireOp",EDGE,"E0.rect.left");var subQ11=sQuery(id+"F0.wireOp",EDGE,"E0.rect.right");var subQ12=sQuery(id+"F0.wireOp",EDGE,"E5.rect.left");Q0=makeQuery(id+"F7.boolean.opBoolean","MERGE",FACE,{"derivedFrom":[makeQuery(id+"F3.boolean.opBoolean","SPLIT",FACE,{"disambiguationData":[TD([makeQuery(id+"F1.opExtrude","SWEPT_FACE",FACE,{"disambiguationData":[OSD([subQ7])]})])],"derivedFrom":makeQuery(id+"F1.opExtrude","CAP_FACE",FACE,{"disambiguationData":[OSD([subQ7,subQ9,subQ10,subQ11,subQ5,subQ4,subQ3,subQ8,subQ2,subQ6,subQ12])],"isStart":false})}),makeQuery(id+"F7.opExtrude","CAP_FACE",FACE,{"disambiguationData":[OSD([subQ1,subQ0,sQuery(id+"F6.wireOp",EDGE,"E35.rect.right")])],"isStart":false}),makeQuery(id+"F7.opExtrude","CAP_FACE",FACE,{"disambiguationData":[OSD([subQ1,subQ0,sQuery(id+"F6.wireOp",EDGE,"E35.rect.left")])],"isStart":false})]});}
            var sketch = newSketch(context, id + "F41", { "sketchPlane" : qUnion([Q0])});
            skLineSegment(sketch, "E77.bottom", {"start": v(-51, 50) * mm, "end": v(-45, 50) * mm});
            skLineSegment(sketch, "E77.top", {"start": v(-51, 44) * mm, "end": v(-45, 44) * mm});
            skLineSegment(sketch, "E77.left", {"start": v(-51, 50) * mm, "end": v(-51, 44) * mm});
            skLineSegment(sketch, "E77.right", {"start": v(-45, 50) * mm, "end": v(-45, 44) * mm});
            skLineSegment(sketch, "E78.bottom", {"start": v(-51, -34) * mm, "end": v(-45, -34) * mm});
            skLineSegment(sketch, "E78.top", {"start": v(-51, -40) * mm, "end": v(-45, -40) * mm});
            skLineSegment(sketch, "E78.left", {"start": v(-51, -34) * mm, "end": v(-51, -40) * mm});
            skLineSegment(sketch, "E78.right", {"start": v(-45, -34) * mm, "end": v(-45, -40) * mm});
            skSolve(sketch);
        }
        {
            var Q0;
            Q0=makeQuery(id+"F41.imprint","IMPRINT",FACE,{"disambiguationData":[TD([[makeQuery(id+"F41.imprint","IMPRINT",EDGE,{"derivedFrom":sQuery(id+"F41.wireOp",EDGE,"E77.bottom")}),-1.0]])]});
            var Q1;
            Q1=makeQuery(id+"F41.imprint","IMPRINT",FACE,{"disambiguationData":[TD([[makeQuery(id+"F41.imprint","IMPRINT",EDGE,{"derivedFrom":sQuery(id+"F41.wireOp",EDGE,"E78.bottom")}),-1.0]])]});
            extrude(context, id + "F42", {"entities" : qUnion([Q0, Q1]), "operationType" : NewBodyOperationType.ADD, "depth" : 9.5 * mm});
        }
        {
            var Q0;
            Q0=makeQuery(id+"F42.opExtrude","SWEPT_FACE",FACE,{"disambiguationData":[OSD([sQuery(id+"F41.wireOp",EDGE,"E78.left")])]});
            var sketch = newSketch(context, id + "F43", { "sketchPlane" : qUnion([Q0])});
            skCircle(sketch, "E79", {"center": v(37, 6.5) * mm, "radius": 1.5 * mm});
            skSolve(sketch);
        }
        {
            var Q0;
            Q0=makeQuery(id+"F43.imprint","IMPRINT",FACE,{"disambiguationData":[TD([[makeQuery(id+"F43.imprint","IMPRINT",EDGE,{"derivedFrom":sQuery(id+"F43.wireOp",EDGE,"E79")}),1.0]])]});
            extrude(context, id + "F44", {"entities" : qUnion([Q0]), "operationType" : NewBodyOperationType.REMOVE, "oppositeDirection" : true, "depth" : 5 * mm});
        }
        {
            var Q0;
            Q0=makeQuery(id+"F42.opExtrude","SWEPT_FACE",FACE,{"disambiguationData":[OSD([sQuery(id+"F41.wireOp",EDGE,"E77.left")])]});
            var sketch = newSketch(context, id + "F45", { "sketchPlane" : qUnion([Q0])});
            skCircle(sketch, "E80", {"center": v(-47, 6.5) * mm, "radius": 1.5 * mm});
            skSolve(sketch);
        }
        {
            var Q0;
            Q0=makeQuery(id+"F45.imprint","IMPRINT",FACE,{"disambiguationData":[TD([[makeQuery(id+"F45.imprint","IMPRINT",EDGE,{"derivedFrom":sQuery(id+"F45.wireOp",EDGE,"E80")}),1.0]])]});
            extrude(context, id + "F46", {"entities" : qUnion([Q0]), "operationType" : NewBodyOperationType.REMOVE, "oppositeDirection" : true, "depth" : 5 * mm});
        }
    });
